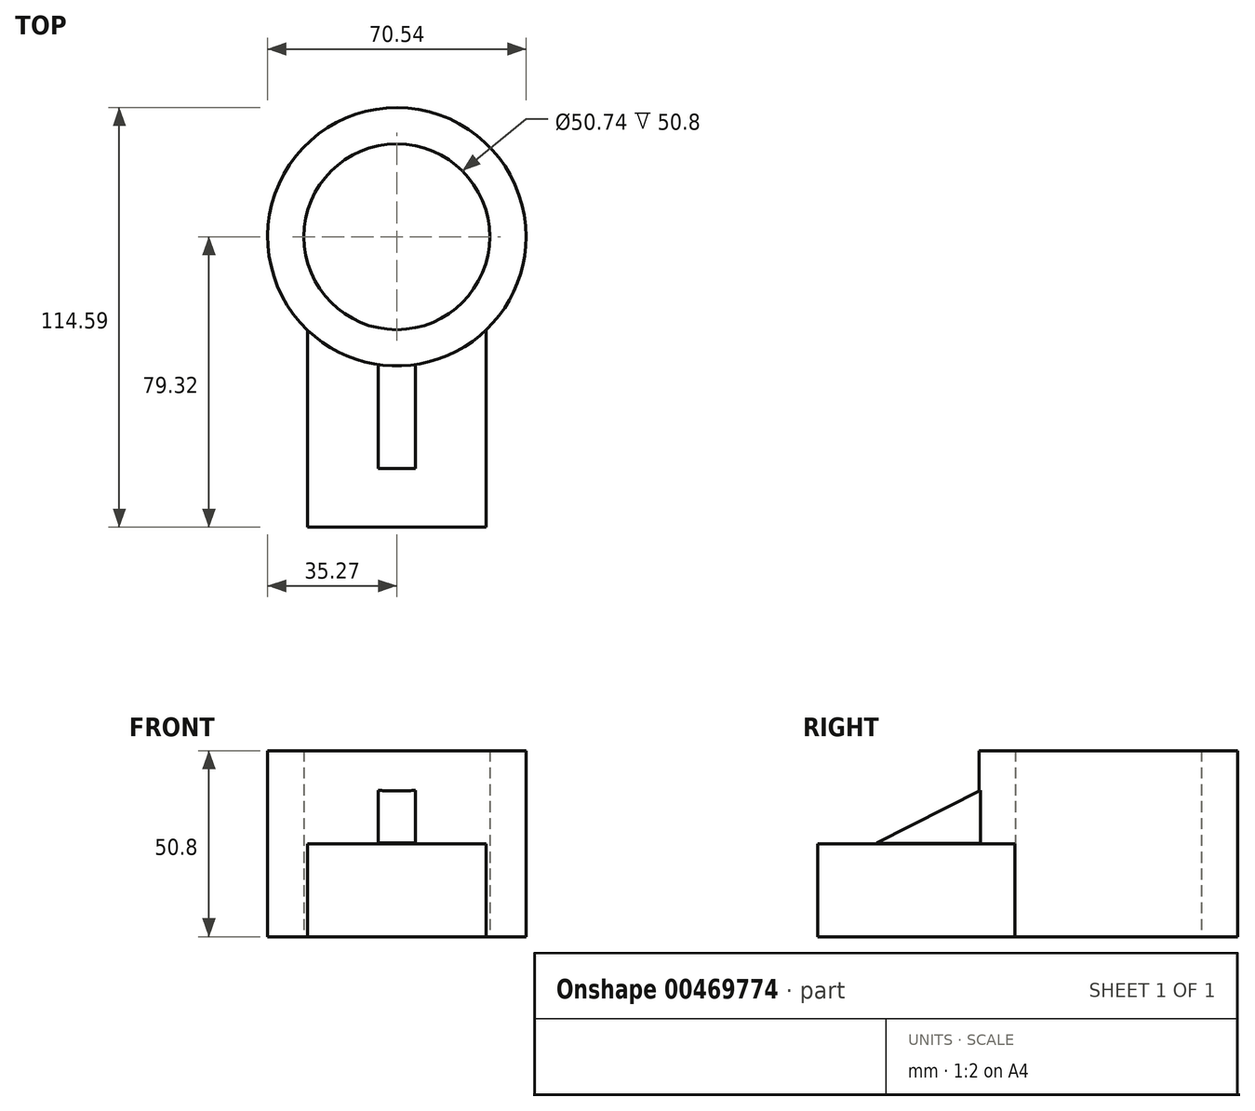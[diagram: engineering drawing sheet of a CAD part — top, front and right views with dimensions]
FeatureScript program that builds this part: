
annotation { "Feature Type Name" : "Feature", "Feature Type Description" : "" }
export const myFeature = defineFeature(function(context is Context, id is Id, definition is map)
    precondition{}
    {
        {
            var Q0;
            Q0=qCreatedBy(makeId("Top.planeOp"),FACE);
            var sketch = newSketch(context, id + "F0", { "sketchPlane" : qUnion([Q0])});
            skCircle(sketch, "E0", {"center": v(0, 35.27) * mm, "radius": 35.27 * mm});
            skCircle(sketch, "E1", {"center": v(0, 35.27) * mm, "radius": 25.37 * mm});
            skSolve(sketch);
        }
        {
            var Q0;
            Q0=makeQuery(id+"F0.imprint","IMPRINT",FACE,{"disambiguationData":[TD([[makeQuery(id+"F0.imprint","IMPRINT",EDGE,{"derivedFrom":sQuery(id+"F0.wireOp",EDGE,"E0")}),1.0]])]});
            extrude(context, id + "F1", {"entities" : qUnion([Q0]), "depth" : 50.8 * mm});
        }
        {
            var Q0;
            Q0=qCreatedBy(makeId("Top.planeOp"),FACE);
            var sketch = newSketch(context, id + "F2", { "sketchPlane" : qUnion([Q0])});
            skLineSegment(sketch, "E2.bottom", {"start": v(-24.43, 9.74) * mm, "end": v(24.43, 9.74) * mm});
            skLineSegment(sketch, "E2.top", {"start": v(-24.43, -44.05) * mm, "end": v(24.43, -44.05) * mm});
            skLineSegment(sketch, "E2.left", {"start": v(-24.43, 9.74) * mm, "end": v(-24.43, -44.05) * mm});
            skLineSegment(sketch, "E2.right", {"start": v(24.43, 9.74) * mm, "end": v(24.43, -44.05) * mm});
            skPoint(sketch, "E2.middle", {"position": v(0, -17.15) * mm});
            skSolve(sketch);
        }
        {
            var Q0;
            Q0=makeQuery(id+"F2.imprint","IMPRINT",FACE,{"disambiguationData":[TD([[makeQuery(id+"F2.imprint","IMPRINT",EDGE,{"derivedFrom":sQuery(id+"F2.wireOp",EDGE,"E2.bottom")}),-1.0]])]});
            extrude(context, id + "F3", {"entities" : qUnion([Q0]), "operationType" : NewBodyOperationType.ADD, "depth" : 25.4 * mm});
        }
        {
            var Q0;
            Q0=qCreatedBy(makeId("Right.planeOp"),FACE);
            var sketch = newSketch(context, id + "F4", { "sketchPlane" : qUnion([Q0])});
            skLineSegment(sketch, "E3", {"start": v(4.12, 25.39) * mm, "end": v(4.12, 41.86) * mm});
            skLineSegment(sketch, "E4", {"start": v(4.12, 41.86) * mm, "end": v(-28, 25.66) * mm});
            skLineSegment(sketch, "E5", {"start": v(-28, 25.66) * mm, "end": v(4.12, 25.39) * mm});
            skSolve(sketch);
        }
        {
            var Q0;
            Q0=makeQuery(id+"F4.imprint","IMPRINT",FACE,{"disambiguationData":[TD([[makeQuery(id+"F4.imprint","IMPRINT",EDGE,{"derivedFrom":sQuery(id+"F4.wireOp",EDGE,"E3")}),1.0]])]});
            extrude(context, id + "F5", {"entities" : qUnion([Q0]), "operationType" : NewBodyOperationType.ADD, "endBound" : BoundingType.SYMMETRIC, "depth" : 10.16 * mm});
        }
    });
